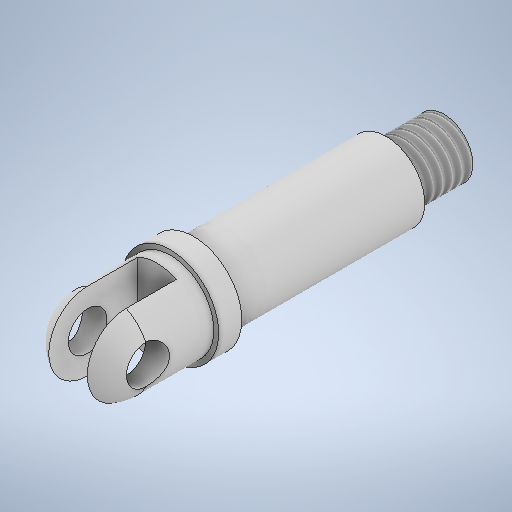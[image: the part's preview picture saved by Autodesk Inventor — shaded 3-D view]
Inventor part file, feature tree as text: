
AUTODESK INVENTOR PART (.ipt)
format: ipt  version: 2025.1 (Build 291241000, 241)  size: 318,976 bytes
history: native  units: mm
features: sketch x3, plane x2, revolve x1, extrude x1, hole x1, thread x1
ambient origin geometry x8: Origin, YZ Plane, XZ Plane, XY Plane, X Axis, Y Axis, Z Axis, Center Point
bodies: Solid1 (feature_tree)
feature tree (9):
  revolve  "Revolution1"  [1 undecoded]
  plane  "Work Plane4"
  extrude  "Extrusion1"  Depth=6.0mm
  plane  "Work Plane5"
  hole  "Hole1"  [1 undecoded]
  thread  "Thread1"  [1 undecoded]
  sketch  "Sketch1"  dims[d0=4.5mm d5=8.0mm]
  sketch  "Sketch2"  dims[d6=20.0mm d7=6.0mm]
  sketch  "Sketch3"  dims[d8=6.0mm d10=10.0mm d11=35.0mm d12=6.6mm d13=90.0deg d17=0.0mm d18=4.0mm d19=2.0mm d20=9.7mm d21=10.0mm d22=0.0mm d23=4.5mm d24=4.0mm d25=6.0mm d26=4.0mm d27=2.0mm d28=90.0deg d29=8.0mm d30=0.0mm d31=8.0mm d32=0.0mm]
note: 3 required parameter values undecoded (feature->parameter linkage not recoverable at this tier; creation-order binding heuristic only, values carry confidence <= 0.55)